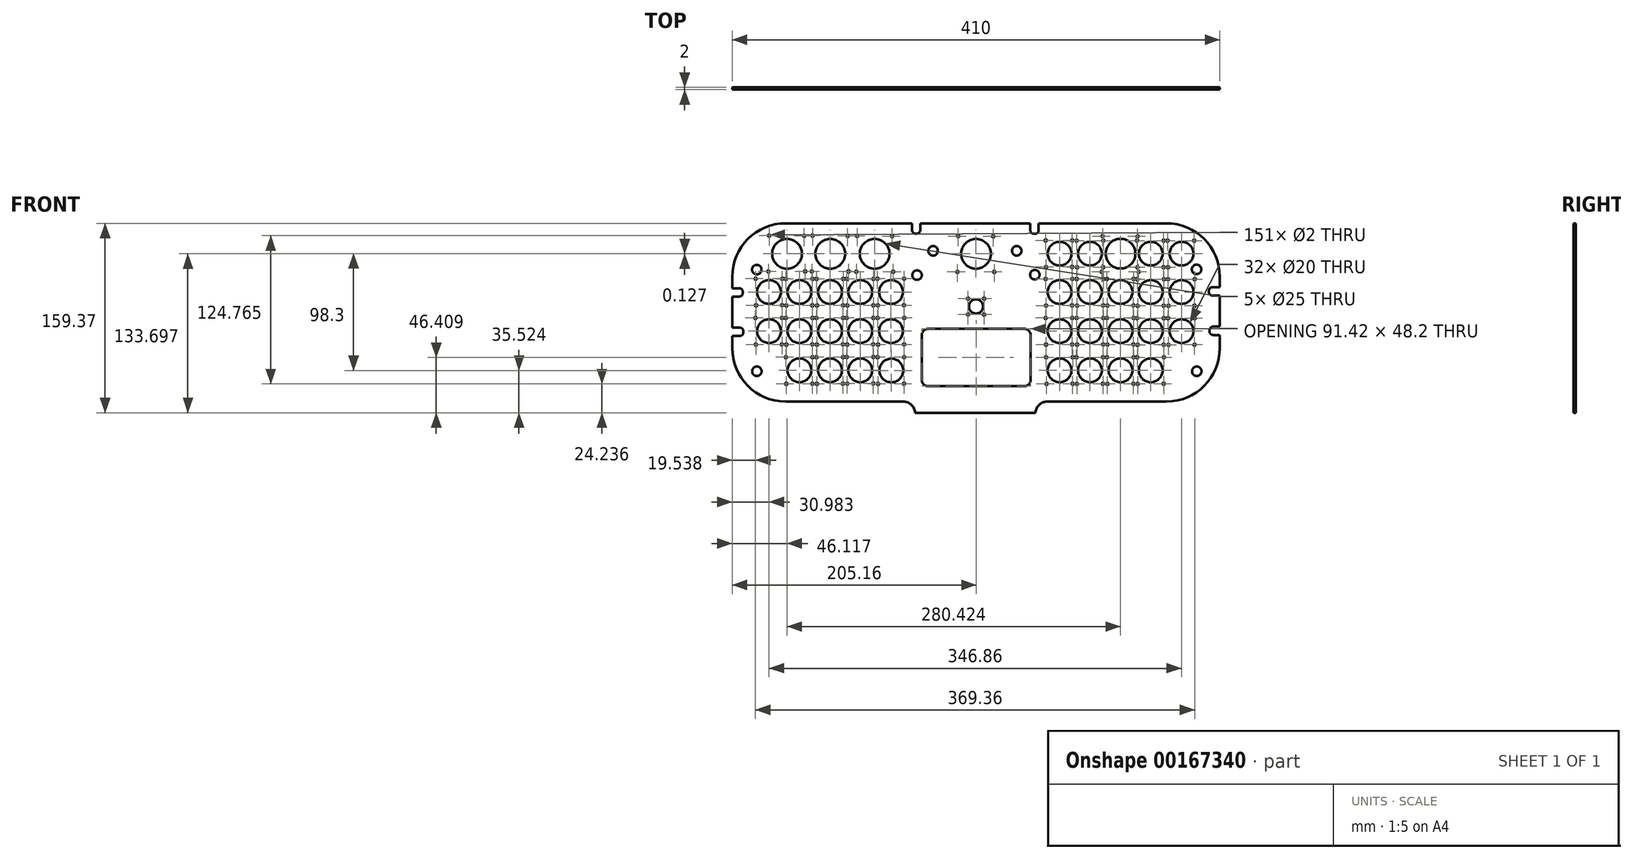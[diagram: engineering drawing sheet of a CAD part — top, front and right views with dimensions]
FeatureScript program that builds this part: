
annotation { "Feature Type Name" : "Feature", "Feature Type Description" : "" }
export const myFeature = defineFeature(function(context is Context, id is Id, definition is map)
    precondition{}
    {
        {
            var Q0;
            Q0=qCreatedBy(makeId("Front.planeOp"),FACE);
            var sketch = newSketch(context, id + "F0", { "sketchPlane" : qUnion([Q0])});
            skLineSegment(sketch, "E0.bottom", {"start": v(205, -75) * mm, "end": v(-205, -75) * mm});
            skLineSegment(sketch, "E0.top", {"start": v(205, 75) * mm, "end": v(-205, 75) * mm});
            skLineSegment(sketch, "E0.left", {"start": v(205, -75) * mm, "end": v(205, 75) * mm});
            skLineSegment(sketch, "E0.right", {"start": v(-205, -75) * mm, "end": v(-205, 75) * mm});
            skSolve(sketch);
        }
        {
            var Q0;
            Q0=qSketchRegion(id+"F0",true);
            extrude(context, id + "F1", {"entities" : qUnion([Q0]), "depth" : 1 * mm, "hasSecondDirection" : true, "secondDirectionOppositeDirection" : true, "secondDirectionDepth" : 1 * mm});
        }
        {
            var Q0;
            Q0=makeQuery(id+"F1.opExtrude","SWEPT_EDGE",EDGE,{"disambiguationData":[OSD([sQuery(id+"F0.wireOp",EDGE,"E0.top"),sQuery(id+"F0.wireOp",EDGE,"E0.right")])]});
            var Q1;
            Q1=makeQuery(id+"F1.opExtrude","SWEPT_EDGE",EDGE,{"disambiguationData":[OSD([sQuery(id+"F0.wireOp",EDGE,"E0.bottom"),sQuery(id+"F0.wireOp",EDGE,"E0.right")])]});
            fillet(context, id + "F2", {"entities" : qUnion([Q0, Q1]), "radius" : 45 * mm, "tangentPropagation" : true, "allowEdgeOverflow" : false});
        }
        {
            var Q0;
            Q0=makeQuery(id+"F1.opExtrude","SWEPT_EDGE",EDGE,{"disambiguationData":[OSD([sQuery(id+"F0.wireOp",EDGE,"E0.top"),sQuery(id+"F0.wireOp",EDGE,"E0.left")])]});
            fillet(context, id + "F3", {"entities" : qUnion([Q0]), "radius" : 45 * mm, "tangentPropagation" : true, "allowEdgeOverflow" : false});
        }
        {
            var Q0;
            Q0=makeQuery(id+"F1.opExtrude","SWEPT_EDGE",EDGE,{"disambiguationData":[OSD([sQuery(id+"F0.wireOp",EDGE,"E0.bottom"),sQuery(id+"F0.wireOp",EDGE,"E0.left")])]});
            fillet(context, id + "F4", {"entities" : qUnion([Q0]), "radius" : 45 * mm, "tangentPropagation" : true, "allowEdgeOverflow" : false});
        }
        {
            var Q0;
            Q0=qCreatedBy(makeId("Front.planeOp"),FACE);
            var sketch = newSketch(context, id + "F5", { "sketchPlane" : qUnion([Q0])});
            skLineSegment(sketch, "E1.bottom", {"start": v(-51.28, -63.48) * mm, "end": v(50, -63.48) * mm});
            skLineSegment(sketch, "E1.top", {"start": v(-51.28, -84.37) * mm, "end": v(50, -84.37) * mm});
            skLineSegment(sketch, "E1.left", {"start": v(-51.28, -63.48) * mm, "end": v(-51.28, -84.37) * mm});
            skLineSegment(sketch, "E1.right", {"start": v(50, -63.48) * mm, "end": v(50, -84.37) * mm});
            skSolve(sketch);
        }
        {
            var Q0;
            Q0=qSketchRegion(id+"F5",true);
            extrude(context, id + "F6", {"entities" : qUnion([Q0]), "operationType" : NewBodyOperationType.ADD, "depth" : 1 * mm, "hasSecondDirection" : true, "secondDirectionOppositeDirection" : true, "secondDirectionDepth" : 1 * mm});
        }
        {
            var Q0;
            Q0=makeQuery(id+"F6.boolean.opBoolean","INTERSECT",EDGE,{"derivedFrom":[makeQuery(id+"F1.opExtrude","SWEPT_FACE",FACE,{"disambiguationData":[OSD([sQuery(id+"F0.wireOp",EDGE,"E0.bottom")])]}),makeQuery(id+"F6.opExtrude","SWEPT_FACE",FACE,{"disambiguationData":[OSD([sQuery(id+"F5.wireOp",EDGE,"E1.left")])]})]});
            fillet(context, id + "F7", {"entities" : qUnion([Q0]), "radius" : 10 * mm, "tangentPropagation" : true, "allowEdgeOverflow" : false});
        }
        {
            var Q0;
            Q0=makeQuery(id+"F6.boolean.opBoolean","INTERSECT",EDGE,{"derivedFrom":[makeQuery(id+"F1.opExtrude","SWEPT_FACE",FACE,{"disambiguationData":[OSD([sQuery(id+"F0.wireOp",EDGE,"E0.bottom")])]}),makeQuery(id+"F6.opExtrude","SWEPT_FACE",FACE,{"disambiguationData":[OSD([sQuery(id+"F5.wireOp",EDGE,"E1.right")])]})]});
            fillet(context, id + "F8", {"entities" : qUnion([Q0]), "radius" : 10 * mm, "tangentPropagation" : true, "allowEdgeOverflow" : false});
        }
        {
            var Q0;
            Q0=qCreatedBy(makeId("Front.planeOp"),FACE);
            var sketch = newSketch(context, id + "F9", { "sketchPlane" : qUnion([Q0])});
            skCircle(sketch, "E2", {"center": v(0, 49.33) * mm, "radius": 12.5 * mm});
            skCircle(sketch, "E3", {"center": v(0, 5.03) * mm, "radius": 6 * mm});
            skCircle(sketch, "E4", {"center": v(-158.88, 49.33) * mm, "radius": 12.5 * mm});
            skCircle(sketch, "E5", {"center": v(-122.54, 49.33) * mm, "radius": 12.5 * mm});
            skCircle(sketch, "E6", {"center": v(-85.24, 49.33) * mm, "radius": 12.5 * mm});
            skCircle(sketch, "E7", {"center": v(172.84, 17.2) * mm, "radius": 10 * mm});
            skCircle(sketch, "E8", {"center": v(172.84, -15.76) * mm, "radius": 10 * mm});
            skCircle(sketch, "E9", {"center": v(146.94, -48.73) * mm, "radius": 10 * mm});
            skCircle(sketch, "E10", {"center": v(146.94, 17.2) * mm, "radius": 10 * mm});
            skCircle(sketch, "E11", {"center": v(146.94, -15.76) * mm, "radius": 10 * mm});
            skCircle(sketch, "E12", {"center": v(121.54, -48.73) * mm, "radius": 10 * mm});
            skCircle(sketch, "E13", {"center": v(121.54, 17.2) * mm, "radius": 10 * mm});
            skCircle(sketch, "E14", {"center": v(121.54, -15.76) * mm, "radius": 10 * mm});
            skCircle(sketch, "E15", {"center": v(95.83, -48.73) * mm, "radius": 10 * mm});
            skCircle(sketch, "E16", {"center": v(95.83, 17.2) * mm, "radius": 10 * mm});
            skCircle(sketch, "E17", {"center": v(95.83, -15.76) * mm, "radius": 10 * mm});
            skCircle(sketch, "E18", {"center": v(70.27, -48.73) * mm, "radius": 10 * mm});
            skCircle(sketch, "E19", {"center": v(70.27, 17.2) * mm, "radius": 10 * mm});
            skCircle(sketch, "E20", {"center": v(70.27, -15.76) * mm, "radius": 10 * mm});
            skCircle(sketch, "E21", {"center": v(172.84, 49.45) * mm, "radius": 10 * mm});
            skCircle(sketch, "E22", {"center": v(146.94, 49.45) * mm, "radius": 10 * mm});
            skCircle(sketch, "E23", {"center": v(121.54, 49.45) * mm, "radius": 12.5 * mm});
            skCircle(sketch, "E24", {"center": v(95.83, 49.45) * mm, "radius": 10 * mm});
            skCircle(sketch, "E25", {"center": v(70.27, 49.45) * mm, "radius": 10 * mm});
            skCircle(sketch, "E26", {"center": v(-71.45, 17.2) * mm, "radius": 10 * mm});
            skCircle(sketch, "E27", {"center": v(-71.45, -15.76) * mm, "radius": 10 * mm});
            skCircle(sketch, "E28", {"center": v(-97.35, -48.73) * mm, "radius": 10 * mm});
            skCircle(sketch, "E29", {"center": v(-97.35, 17.2) * mm, "radius": 10 * mm});
            skCircle(sketch, "E30", {"center": v(-97.35, -15.76) * mm, "radius": 10 * mm});
            skCircle(sketch, "E31", {"center": v(-122.75, -48.73) * mm, "radius": 10 * mm});
            skCircle(sketch, "E32", {"center": v(-122.75, 17.2) * mm, "radius": 10 * mm});
            skCircle(sketch, "E33", {"center": v(-122.75, -15.76) * mm, "radius": 10 * mm});
            skCircle(sketch, "E34", {"center": v(-148.46, -48.73) * mm, "radius": 10 * mm});
            skCircle(sketch, "E35", {"center": v(-148.46, 17.2) * mm, "radius": 10 * mm});
            skCircle(sketch, "E36", {"center": v(-148.46, -15.76) * mm, "radius": 10 * mm});
            skCircle(sketch, "E37", {"center": v(-174.02, 17.2) * mm, "radius": 10 * mm});
            skCircle(sketch, "E38", {"center": v(-174.02, -15.76) * mm, "radius": 10 * mm});
            skCircle(sketch, "E39", {"center": v(-71.2, -48.85) * mm, "radius": 10 * mm});
            skLineSegment(sketch, "E40.bottom", {"start": v(-45.55, -13.86) * mm, "end": v(45.87, -13.86) * mm});
            skLineSegment(sketch, "E40.top", {"start": v(-45.55, -62.06) * mm, "end": v(45.87, -62.06) * mm});
            skLineSegment(sketch, "E40.left", {"start": v(-45.55, -13.86) * mm, "end": v(-45.55, -62.06) * mm});
            skLineSegment(sketch, "E40.right", {"start": v(45.87, -13.86) * mm, "end": v(45.87, -62.06) * mm});
            skSolve(sketch);
        }
        {
            var Q0;
            Q0=makeQuery(id+"F6.boolean.opBoolean","MERGE",FACE,{"derivedFrom":[makeQuery(id+"F1.opExtrude","CAP_FACE",FACE,{"disambiguationData":[OSD([sQuery(id+"F0.wireOp",EDGE,"E0.bottom"),sQuery(id+"F0.wireOp",EDGE,"E0.top"),sQuery(id+"F0.wireOp",EDGE,"E0.left"),sQuery(id+"F0.wireOp",EDGE,"E0.right")])],"isStart":false}),makeQuery(id+"F6.opExtrude","CAP_FACE",FACE,{"disambiguationData":[OSD([sQuery(id+"F5.wireOp",EDGE,"E1.bottom"),sQuery(id+"F5.wireOp",EDGE,"E1.top"),sQuery(id+"F5.wireOp",EDGE,"E1.left"),sQuery(id+"F5.wireOp",EDGE,"E1.right")])],"isStart":false})]});
            cPlane(context, id + "F10", {"entities" : qUnion([Q0]), "cplaneType" : CPlaneType.OFFSET, "offset" : 0 * mm, "width" : 150 * mm, "height" : 150 * mm});
        }
        {
            var Q0;
            Q0=qCreatedBy(id+"F10.planeOp",FACE);
            var sketch = newSketch(context, id + "F11", { "sketchPlane" : qUnion([Q0])});
            skLineSegment(sketch, "E41.bottom", {"start": v(-210.38, 20.36) * mm, "end": v(-199.13, 20.36) * mm});
            skLineSegment(sketch, "E41.top", {"start": v(-210.38, 13.36) * mm, "end": v(-199.13, 13.36) * mm});
            skLineSegment(sketch, "E41.left", {"start": v(-213.38, 17.36) * mm, "end": v(-213.38, 16.36) * mm});
            skLineSegment(sketch, "E41.right", {"start": v(-196.13, 17.36) * mm, "end": v(-196.13, 16.36) * mm});
            skPoint(sketch, "E42.visualSharp", {"position": v(-196.13, 20.36) * mm});
            skArc(sketch, "E42.filletArc", {"start": v(-196.13, 17.36) * mm, "mid": v(-197.01, 19.48) * mm, "end": v(-199.13, 20.36) * mm});
            skPoint(sketch, "E43.visualSharp", {"position": v(-196.13, 13.36) * mm});
            skArc(sketch, "E43.filletArc", {"start": v(-199.13, 13.36) * mm, "mid": v(-197.01, 14.23) * mm, "end": v(-196.13, 16.36) * mm});
            skPoint(sketch, "E44.visualSharp", {"position": v(-213.38, 20.36) * mm});
            skArc(sketch, "E44.filletArc", {"start": v(-210.38, 20.36) * mm, "mid": v(-212.5, 19.48) * mm, "end": v(-213.38, 17.36) * mm});
            skPoint(sketch, "E45.visualSharp", {"position": v(-213.38, 13.36) * mm});
            skArc(sketch, "E45.filletArc", {"start": v(-213.38, 16.36) * mm, "mid": v(-212.5, 14.23) * mm, "end": v(-210.38, 13.36) * mm});
            skLineSegment(sketch, "E46.bottom", {"start": v(-209.84, -12.8) * mm, "end": v(-198.59, -12.8) * mm});
            skLineSegment(sketch, "E46.top", {"start": v(-209.84, -19.8) * mm, "end": v(-198.59, -19.8) * mm});
            skLineSegment(sketch, "E46.left", {"start": v(-212.84, -15.8) * mm, "end": v(-212.84, -16.8) * mm});
            skLineSegment(sketch, "E46.right", {"start": v(-195.59, -15.8) * mm, "end": v(-195.59, -16.8) * mm});
            skPoint(sketch, "E47.visualSharp", {"position": v(-195.59, -12.8) * mm});
            skArc(sketch, "E47.filletArc", {"start": v(-195.59, -15.8) * mm, "mid": v(-196.47, -13.69) * mm, "end": v(-198.59, -12.8) * mm});
            skPoint(sketch, "E48.visualSharp", {"position": v(-195.59, -19.8) * mm});
            skArc(sketch, "E48.filletArc", {"start": v(-198.59, -19.8) * mm, "mid": v(-196.47, -18.93) * mm, "end": v(-195.59, -16.8) * mm});
            skPoint(sketch, "E49.visualSharp", {"position": v(-212.84, -12.8) * mm});
            skArc(sketch, "E49.filletArc", {"start": v(-209.84, -12.8) * mm, "mid": v(-211.96, -13.69) * mm, "end": v(-212.84, -15.8) * mm});
            skPoint(sketch, "E50.visualSharp", {"position": v(-212.84, -19.8) * mm});
            skArc(sketch, "E50.filletArc", {"start": v(-212.84, -16.8) * mm, "mid": v(-211.96, -18.93) * mm, "end": v(-209.84, -19.8) * mm});
            skLineSegment(sketch, "E51.bottom", {"start": v(198.82, 21.2) * mm, "end": v(210.07, 21.2) * mm});
            skLineSegment(sketch, "E51.top", {"start": v(198.82, 14.2) * mm, "end": v(210.07, 14.2) * mm});
            skLineSegment(sketch, "E51.left", {"start": v(195.82, 18.2) * mm, "end": v(195.82, 17.2) * mm});
            skLineSegment(sketch, "E51.right", {"start": v(213.07, 18.2) * mm, "end": v(213.07, 17.2) * mm});
            skPoint(sketch, "E52.visualSharp", {"position": v(213.07, 21.2) * mm});
            skArc(sketch, "E52.filletArc", {"start": v(213.07, 18.2) * mm, "mid": v(212.2, 20.32) * mm, "end": v(210.07, 21.2) * mm});
            skPoint(sketch, "E53.visualSharp", {"position": v(213.07, 14.2) * mm});
            skArc(sketch, "E53.filletArc", {"start": v(210.07, 14.2) * mm, "mid": v(212.2, 15.07) * mm, "end": v(213.07, 17.2) * mm});
            skPoint(sketch, "E54.visualSharp", {"position": v(195.82, 21.2) * mm});
            skArc(sketch, "E54.filletArc", {"start": v(198.82, 21.2) * mm, "mid": v(196.7, 20.32) * mm, "end": v(195.82, 18.2) * mm});
            skPoint(sketch, "E55.visualSharp", {"position": v(195.82, 14.2) * mm});
            skArc(sketch, "E55.filletArc", {"start": v(195.82, 17.2) * mm, "mid": v(196.7, 15.07) * mm, "end": v(198.82, 14.2) * mm});
            skLineSegment(sketch, "E56.bottom", {"start": v(199.36, -11.97) * mm, "end": v(210.61, -11.97) * mm});
            skLineSegment(sketch, "E56.top", {"start": v(199.36, -18.97) * mm, "end": v(210.61, -18.97) * mm});
            skLineSegment(sketch, "E56.left", {"start": v(196.36, -14.97) * mm, "end": v(196.36, -15.97) * mm});
            skLineSegment(sketch, "E56.right", {"start": v(213.61, -14.97) * mm, "end": v(213.61, -15.97) * mm});
            skPoint(sketch, "E57.visualSharp", {"position": v(213.61, -11.97) * mm});
            skArc(sketch, "E57.filletArc", {"start": v(213.61, -14.97) * mm, "mid": v(212.73, -12.85) * mm, "end": v(210.61, -11.97) * mm});
            skPoint(sketch, "E58.visualSharp", {"position": v(213.61, -18.97) * mm});
            skArc(sketch, "E58.filletArc", {"start": v(210.61, -18.97) * mm, "mid": v(212.73, -18.1) * mm, "end": v(213.61, -15.97) * mm});
            skPoint(sketch, "E59.visualSharp", {"position": v(196.36, -11.97) * mm});
            skArc(sketch, "E59.filletArc", {"start": v(199.36, -11.97) * mm, "mid": v(197.24, -12.85) * mm, "end": v(196.36, -14.97) * mm});
            skPoint(sketch, "E60.visualSharp", {"position": v(196.36, -18.97) * mm});
            skArc(sketch, "E60.filletArc", {"start": v(196.36, -15.97) * mm, "mid": v(197.24, -18.1) * mm, "end": v(199.36, -18.97) * mm});
            skLineSegment(sketch, "E61.bottom", {"start": v(-50.84, 85.12) * mm, "end": v(-49.84, 85.12) * mm});
            skLineSegment(sketch, "E61.top", {"start": v(-50.84, 66.34) * mm, "end": v(-49.84, 66.34) * mm});
            skLineSegment(sketch, "E61.left", {"start": v(-53.84, 82.12) * mm, "end": v(-53.84, 69.34) * mm});
            skLineSegment(sketch, "E61.right", {"start": v(-46.84, 82.12) * mm, "end": v(-46.84, 69.34) * mm});
            skPoint(sketch, "E62.visualSharp", {"position": v(-53.84, 85.12) * mm});
            skArc(sketch, "E62.filletArc", {"start": v(-50.84, 85.12) * mm, "mid": v(-52.96, 84.24) * mm, "end": v(-53.84, 82.12) * mm});
            skPoint(sketch, "E63.visualSharp", {"position": v(-46.84, 85.12) * mm});
            skArc(sketch, "E63.filletArc", {"start": v(-46.84, 82.12) * mm, "mid": v(-47.72, 84.24) * mm, "end": v(-49.84, 85.12) * mm});
            skPoint(sketch, "E64.visualSharp", {"position": v(-46.84, 66.34) * mm});
            skArc(sketch, "E64.filletArc", {"start": v(-49.84, 66.34) * mm, "mid": v(-47.72, 67.22) * mm, "end": v(-46.84, 69.34) * mm});
            skPoint(sketch, "E65.visualSharp", {"position": v(-53.84, 66.34) * mm});
            skArc(sketch, "E65.filletArc", {"start": v(-53.84, 69.34) * mm, "mid": v(-52.96, 67.22) * mm, "end": v(-50.84, 66.34) * mm});
            skLineSegment(sketch, "E66.bottom", {"start": v(48.7, 84.97) * mm, "end": v(49.7, 84.97) * mm});
            skLineSegment(sketch, "E66.top", {"start": v(48.7, 66.19) * mm, "end": v(49.7, 66.19) * mm});
            skLineSegment(sketch, "E66.left", {"start": v(45.7, 81.97) * mm, "end": v(45.7, 69.19) * mm});
            skLineSegment(sketch, "E66.right", {"start": v(52.7, 81.97) * mm, "end": v(52.7, 69.19) * mm});
            skPoint(sketch, "E67.visualSharp", {"position": v(45.7, 84.97) * mm});
            skArc(sketch, "E67.filletArc", {"start": v(48.7, 84.97) * mm, "mid": v(46.57, 84.09) * mm, "end": v(45.7, 81.97) * mm});
            skPoint(sketch, "E68.visualSharp", {"position": v(52.7, 84.97) * mm});
            skArc(sketch, "E68.filletArc", {"start": v(52.7, 81.97) * mm, "mid": v(51.81, 84.09) * mm, "end": v(49.7, 84.97) * mm});
            skPoint(sketch, "E69.visualSharp", {"position": v(52.7, 66.19) * mm});
            skArc(sketch, "E69.filletArc", {"start": v(49.7, 66.19) * mm, "mid": v(51.81, 67.07) * mm, "end": v(52.7, 69.19) * mm});
            skPoint(sketch, "E70.visualSharp", {"position": v(45.7, 66.19) * mm});
            skArc(sketch, "E70.filletArc", {"start": v(45.7, 69.19) * mm, "mid": v(46.57, 67.07) * mm, "end": v(48.7, 66.19) * mm});
            skSolve(sketch);
        }
        {
            var Q0;
            Q0=makeQuery(id+"F6.boolean.opBoolean","MERGE",FACE,{"derivedFrom":[makeQuery(id+"F1.opExtrude","CAP_FACE",FACE,{"disambiguationData":[OSD([sQuery(id+"F0.wireOp",EDGE,"E0.bottom"),sQuery(id+"F0.wireOp",EDGE,"E0.top"),sQuery(id+"F0.wireOp",EDGE,"E0.left"),sQuery(id+"F0.wireOp",EDGE,"E0.right")])],"isStart":false}),makeQuery(id+"F6.opExtrude","CAP_FACE",FACE,{"disambiguationData":[OSD([sQuery(id+"F5.wireOp",EDGE,"E1.bottom"),sQuery(id+"F5.wireOp",EDGE,"E1.top"),sQuery(id+"F5.wireOp",EDGE,"E1.left"),sQuery(id+"F5.wireOp",EDGE,"E1.right")])],"isStart":false})]});
            cPlane(context, id + "F12", {"entities" : qUnion([Q0]), "cplaneType" : CPlaneType.OFFSET, "offset" : 2 * mm, "oppositeDirection" : true, "width" : 150 * mm, "height" : 150 * mm});
        }
        {
            var Q0;
            Q0=qCreatedBy(id+"F12.planeOp",FACE);
            var sketch = newSketch(context, id + "F13", { "sketchPlane" : qUnion([Q0])});
            skCircle(sketch, "E71", {"center": v(-184.3, 36.01) * mm, "radius": 4 * mm});
            skCircle(sketch, "E72", {"center": v(-184.28, -49.46) * mm, "radius": 4 * mm});
            skCircle(sketch, "E73", {"center": v(-36.07, 51.83) * mm, "radius": 4 * mm});
            skCircle(sketch, "E74", {"center": v(-49.57, 31.39) * mm, "radius": 4 * mm});
            skCircle(sketch, "E75", {"center": v(34.27, 51.83) * mm, "radius": 4 * mm});
            skCircle(sketch, "E76", {"center": v(49.46, 31.76) * mm, "radius": 4 * mm});
            skCircle(sketch, "E77", {"center": v(185.45, 36.26) * mm, "radius": 4 * mm});
            skCircle(sketch, "E78", {"center": v(185.64, -49.46) * mm, "radius": 4 * mm});
            skSolve(sketch);
        }
        {
            var Q0;
            Q0=qSketchRegion(id+"F13",true);
            extrude(context, id + "F14", {"entities" : qUnion([Q0]), "operationType" : NewBodyOperationType.REMOVE, "depth" : 28.49 * mm, "hasSecondDirection" : true, "secondDirectionOppositeDirection" : true, "secondDirectionDepth" : 25 * mm});
        }
        {
            var Q0;
            Q0=qSketchRegion(id+"F9",true);
            extrude(context, id + "F15", {"entities" : qUnion([Q0]), "operationType" : NewBodyOperationType.REMOVE, "depth" : 25 * mm, "hasSecondDirection" : true, "secondDirectionOppositeDirection" : true, "secondDirectionDepth" : 25 * mm});
        }
        {
            var Q0;
            Q0=qSketchRegion(id+"F11",true);
            extrude(context, id + "F16", {"entities" : qUnion([Q0]), "operationType" : NewBodyOperationType.REMOVE, "oppositeDirection" : true, "depth" : 50 * mm, "hasSecondDirection" : true, "secondDirectionOppositeDirection" : false, "secondDirectionDepth" : 50 * mm});
        }
        {
            var Q0;
            Q0=makeQuery(id+"F6.boolean.opBoolean","MERGE",FACE,{"derivedFrom":[makeQuery(id+"F1.opExtrude","CAP_FACE",FACE,{"disambiguationData":[OSD([sQuery(id+"F0.wireOp",EDGE,"E0.bottom"),sQuery(id+"F0.wireOp",EDGE,"E0.top"),sQuery(id+"F0.wireOp",EDGE,"E0.left"),sQuery(id+"F0.wireOp",EDGE,"E0.right")])],"isStart":true}),makeQuery(id+"F6.opExtrude","CAP_FACE",FACE,{"disambiguationData":[OSD([sQuery(id+"F5.wireOp",EDGE,"E1.bottom"),sQuery(id+"F5.wireOp",EDGE,"E1.top"),sQuery(id+"F5.wireOp",EDGE,"E1.left"),sQuery(id+"F5.wireOp",EDGE,"E1.right")])],"isStart":true})]});
            cPlane(context, id + "F17", {"entities" : qUnion([Q0]), "cplaneType" : CPlaneType.OFFSET, "offset" : 0 * mm, "oppositeDirection" : true, "width" : 150 * mm, "height" : 150 * mm});
        }
        {
            var Q0;
            Q0=qCreatedBy(id+"F17.planeOp",FACE);
            var sketch = newSketch(context, id + "F18", { "sketchPlane" : qUnion([Q0])});
            skLineSegment(sketch, "E79.bottom", {"start": v(184.07, 27.38) * mm, "end": v(163.8, 27.38) * mm, "construction": true});
            skLineSegment(sketch, "E79.top", {"start": v(184.07, 7.22) * mm, "end": v(163.8, 7.22) * mm, "construction": true});
            skLineSegment(sketch, "E79.left", {"start": v(184.07, 27.38) * mm, "end": v(184.07, 7.22) * mm, "construction": true});
            skLineSegment(sketch, "E79.right", {"start": v(163.8, 27.38) * mm, "end": v(163.8, 7.22) * mm, "construction": true});
            skPoint(sketch, "E80", {"position": v(185.32, 28.38) * mm});
            skPoint(sketch, "E81", {"position": v(162.91, 28.38) * mm});
            skPoint(sketch, "E82", {"position": v(184.95, 5.97) * mm});
            skPoint(sketch, "E83", {"position": v(163.04, 6.1) * mm});
            skLineSegment(sketch, "E84.bottom", {"start": v(158.64, 27.26) * mm, "end": v(138.36, 27.26) * mm, "construction": true});
            skLineSegment(sketch, "E84.top", {"start": v(158.64, 7.1) * mm, "end": v(138.36, 7.1) * mm, "construction": true});
            skLineSegment(sketch, "E84.left", {"start": v(158.64, 27.26) * mm, "end": v(158.64, 7.1) * mm, "construction": true});
            skLineSegment(sketch, "E84.right", {"start": v(138.36, 27.26) * mm, "end": v(138.36, 7.1) * mm, "construction": true});
            skPoint(sketch, "E85", {"position": v(159.89, 28.26) * mm});
            skPoint(sketch, "E86", {"position": v(137.48, 28.26) * mm});
            skPoint(sketch, "E87", {"position": v(159.51, 5.85) * mm});
            skPoint(sketch, "E88", {"position": v(137.6, 5.98) * mm});
            skLineSegment(sketch, "E89.bottom", {"start": v(132.78, 27.26) * mm, "end": v(112.5, 27.26) * mm, "construction": true});
            skLineSegment(sketch, "E89.top", {"start": v(132.78, 7.1) * mm, "end": v(112.5, 7.1) * mm, "construction": true});
            skLineSegment(sketch, "E89.left", {"start": v(132.78, 27.26) * mm, "end": v(132.78, 7.1) * mm, "construction": true});
            skLineSegment(sketch, "E89.right", {"start": v(112.5, 27.26) * mm, "end": v(112.5, 7.1) * mm, "construction": true});
            skPoint(sketch, "E90", {"position": v(134.03, 28.26) * mm});
            skPoint(sketch, "E91", {"position": v(111.62, 28.26) * mm});
            skPoint(sketch, "E92", {"position": v(133.66, 5.85) * mm});
            skPoint(sketch, "E93", {"position": v(111.75, 5.98) * mm});
            skLineSegment(sketch, "E94.bottom", {"start": v(107.35, 27.26) * mm, "end": v(87.07, 27.26) * mm, "construction": true});
            skLineSegment(sketch, "E94.top", {"start": v(107.35, 7.1) * mm, "end": v(87.07, 7.1) * mm, "construction": true});
            skLineSegment(sketch, "E94.left", {"start": v(107.35, 27.26) * mm, "end": v(107.35, 7.1) * mm, "construction": true});
            skLineSegment(sketch, "E94.right", {"start": v(87.07, 27.26) * mm, "end": v(87.07, 7.1) * mm, "construction": true});
            skPoint(sketch, "E95", {"position": v(108.6, 28.26) * mm});
            skPoint(sketch, "E96", {"position": v(86.19, 28.26) * mm});
            skPoint(sketch, "E97", {"position": v(108.22, 5.85) * mm});
            skPoint(sketch, "E98", {"position": v(86.31, 5.98) * mm});
            skLineSegment(sketch, "E99.bottom", {"start": v(81.63, 27.4) * mm, "end": v(61.35, 27.4) * mm, "construction": true});
            skLineSegment(sketch, "E99.top", {"start": v(81.63, 7.24) * mm, "end": v(61.35, 7.24) * mm, "construction": true});
            skLineSegment(sketch, "E99.left", {"start": v(81.63, 27.4) * mm, "end": v(81.63, 7.24) * mm, "construction": true});
            skLineSegment(sketch, "E99.right", {"start": v(61.35, 27.4) * mm, "end": v(61.35, 7.24) * mm, "construction": true});
            skPoint(sketch, "E100", {"position": v(82.88, 28.4) * mm});
            skPoint(sketch, "E101", {"position": v(60.47, 28.4) * mm});
            skPoint(sketch, "E102", {"position": v(82.5, 6) * mm});
            skPoint(sketch, "E103", {"position": v(60.6, 6.12) * mm});
            skLineSegment(sketch, "E104.bottom", {"start": v(184.21, -5.62) * mm, "end": v(163.93, -5.62) * mm, "construction": true});
            skLineSegment(sketch, "E104.top", {"start": v(184.21, -25.78) * mm, "end": v(163.93, -25.78) * mm, "construction": true});
            skLineSegment(sketch, "E104.left", {"start": v(184.21, -5.62) * mm, "end": v(184.21, -25.78) * mm, "construction": true});
            skLineSegment(sketch, "E104.right", {"start": v(163.93, -5.62) * mm, "end": v(163.93, -25.78) * mm, "construction": true});
            skPoint(sketch, "E105", {"position": v(185.46, -4.62) * mm});
            skPoint(sketch, "E106", {"position": v(163.05, -4.62) * mm});
            skPoint(sketch, "E107", {"position": v(185.09, -27.03) * mm});
            skPoint(sketch, "E108", {"position": v(163.18, -26.9) * mm});
            skLineSegment(sketch, "E109.bottom", {"start": v(158.64, -5.62) * mm, "end": v(138.36, -5.62) * mm, "construction": true});
            skLineSegment(sketch, "E109.top", {"start": v(158.64, -25.78) * mm, "end": v(138.36, -25.78) * mm, "construction": true});
            skLineSegment(sketch, "E109.left", {"start": v(158.64, -5.62) * mm, "end": v(158.64, -25.78) * mm, "construction": true});
            skLineSegment(sketch, "E109.right", {"start": v(138.36, -5.62) * mm, "end": v(138.36, -25.78) * mm, "construction": true});
            skPoint(sketch, "E110", {"position": v(159.89, -4.62) * mm});
            skPoint(sketch, "E111", {"position": v(137.48, -4.62) * mm});
            skPoint(sketch, "E112", {"position": v(159.51, -27.03) * mm});
            skPoint(sketch, "E113", {"position": v(137.6, -26.9) * mm});
            skLineSegment(sketch, "E114.bottom", {"start": v(132.92, -5.62) * mm, "end": v(112.64, -5.62) * mm, "construction": true});
            skLineSegment(sketch, "E114.top", {"start": v(132.92, -25.78) * mm, "end": v(112.64, -25.78) * mm, "construction": true});
            skLineSegment(sketch, "E114.left", {"start": v(132.92, -5.62) * mm, "end": v(132.92, -25.78) * mm, "construction": true});
            skLineSegment(sketch, "E114.right", {"start": v(112.64, -5.62) * mm, "end": v(112.64, -25.78) * mm, "construction": true});
            skPoint(sketch, "E115", {"position": v(134.17, -4.62) * mm});
            skPoint(sketch, "E116", {"position": v(111.76, -4.62) * mm});
            skPoint(sketch, "E117", {"position": v(133.8, -27.03) * mm});
            skPoint(sketch, "E118", {"position": v(111.89, -26.9) * mm});
            skLineSegment(sketch, "E119.bottom", {"start": v(107.49, -5.62) * mm, "end": v(87.2, -5.62) * mm, "construction": true});
            skLineSegment(sketch, "E119.top", {"start": v(107.49, -25.78) * mm, "end": v(87.2, -25.78) * mm, "construction": true});
            skLineSegment(sketch, "E119.left", {"start": v(107.49, -5.62) * mm, "end": v(107.49, -25.78) * mm, "construction": true});
            skLineSegment(sketch, "E119.right", {"start": v(87.2, -5.62) * mm, "end": v(87.2, -25.78) * mm, "construction": true});
            skPoint(sketch, "E120", {"position": v(108.74, -4.62) * mm});
            skPoint(sketch, "E121", {"position": v(86.33, -4.62) * mm});
            skPoint(sketch, "E122", {"position": v(108.36, -27.03) * mm});
            skPoint(sketch, "E123", {"position": v(86.45, -26.9) * mm});
            skLineSegment(sketch, "E124.bottom", {"start": v(81.5, -5.62) * mm, "end": v(61.2, -5.62) * mm, "construction": true});
            skLineSegment(sketch, "E124.top", {"start": v(81.5, -25.78) * mm, "end": v(61.2, -25.78) * mm, "construction": true});
            skLineSegment(sketch, "E124.left", {"start": v(81.5, -5.62) * mm, "end": v(81.5, -25.78) * mm, "construction": true});
            skLineSegment(sketch, "E124.right", {"start": v(61.2, -5.62) * mm, "end": v(61.2, -25.78) * mm, "construction": true});
            skPoint(sketch, "E125", {"position": v(82.74, -4.62) * mm});
            skPoint(sketch, "E126", {"position": v(60.33, -4.62) * mm});
            skPoint(sketch, "E127", {"position": v(82.37, -27.03) * mm});
            skPoint(sketch, "E128", {"position": v(60.46, -26.9) * mm});
            skLineSegment(sketch, "E129.bottom", {"start": v(158.65, -38.7) * mm, "end": v(138.37, -38.7) * mm, "construction": true});
            skLineSegment(sketch, "E129.top", {"start": v(158.65, -58.85) * mm, "end": v(138.37, -58.85) * mm, "construction": true});
            skLineSegment(sketch, "E129.left", {"start": v(158.65, -38.7) * mm, "end": v(158.65, -58.85) * mm, "construction": true});
            skLineSegment(sketch, "E129.right", {"start": v(138.37, -38.7) * mm, "end": v(138.37, -58.85) * mm, "construction": true});
            skPoint(sketch, "E130", {"position": v(159.9, -37.69) * mm});
            skPoint(sketch, "E131", {"position": v(137.5, -37.69) * mm});
            skPoint(sketch, "E132", {"position": v(159.53, -60.1) * mm});
            skPoint(sketch, "E133", {"position": v(137.62, -59.97) * mm});
            skLineSegment(sketch, "E134.bottom", {"start": v(132.95, -38.7) * mm, "end": v(112.67, -38.7) * mm, "construction": true});
            skLineSegment(sketch, "E134.top", {"start": v(132.95, -58.85) * mm, "end": v(112.67, -58.85) * mm, "construction": true});
            skLineSegment(sketch, "E134.left", {"start": v(132.95, -38.7) * mm, "end": v(132.95, -58.85) * mm, "construction": true});
            skLineSegment(sketch, "E134.right", {"start": v(112.67, -38.7) * mm, "end": v(112.67, -58.85) * mm, "construction": true});
            skPoint(sketch, "E135", {"position": v(134.2, -37.69) * mm});
            skPoint(sketch, "E136", {"position": v(111.8, -37.69) * mm});
            skPoint(sketch, "E137", {"position": v(133.83, -60.1) * mm});
            skPoint(sketch, "E138", {"position": v(111.92, -59.97) * mm});
            skLineSegment(sketch, "E139.bottom", {"start": v(107.44, -38.5) * mm, "end": v(87.16, -38.5) * mm, "construction": true});
            skLineSegment(sketch, "E139.top", {"start": v(107.44, -58.66) * mm, "end": v(87.16, -58.66) * mm, "construction": true});
            skLineSegment(sketch, "E139.left", {"start": v(107.44, -38.5) * mm, "end": v(107.44, -58.66) * mm, "construction": true});
            skLineSegment(sketch, "E139.right", {"start": v(87.16, -38.5) * mm, "end": v(87.16, -58.66) * mm, "construction": true});
            skPoint(sketch, "E140", {"position": v(108.7, -37.5) * mm});
            skPoint(sketch, "E141", {"position": v(86.29, -37.5) * mm});
            skPoint(sketch, "E142", {"position": v(108.32, -59.91) * mm});
            skPoint(sketch, "E143", {"position": v(86.41, -59.79) * mm});
            skLineSegment(sketch, "E144.bottom", {"start": v(81.56, -38.7) * mm, "end": v(61.28, -38.7) * mm, "construction": true});
            skLineSegment(sketch, "E144.top", {"start": v(81.56, -58.85) * mm, "end": v(61.28, -58.85) * mm, "construction": true});
            skLineSegment(sketch, "E144.left", {"start": v(81.56, -38.7) * mm, "end": v(81.56, -58.85) * mm, "construction": true});
            skLineSegment(sketch, "E144.right", {"start": v(61.28, -38.7) * mm, "end": v(61.28, -58.85) * mm, "construction": true});
            skPoint(sketch, "E145", {"position": v(82.8, -37.69) * mm});
            skPoint(sketch, "E146", {"position": v(60.4, -37.69) * mm});
            skPoint(sketch, "E147", {"position": v(82.43, -60.1) * mm});
            skPoint(sketch, "E148", {"position": v(60.53, -59.97) * mm});
            skLineSegment(sketch, "E149.bottom", {"start": v(-59.78, 59.6) * mm, "end": v(-80.07, 59.6) * mm, "construction": true});
            skLineSegment(sketch, "E149.top", {"start": v(-59.78, 39.44) * mm, "end": v(-80.07, 39.44) * mm, "construction": true});
            skLineSegment(sketch, "E149.left", {"start": v(-59.78, 59.6) * mm, "end": v(-59.78, 39.44) * mm, "construction": true});
            skLineSegment(sketch, "E149.right", {"start": v(-80.07, 59.6) * mm, "end": v(-80.07, 39.44) * mm, "construction": true});
            skPoint(sketch, "E150", {"position": v(-58.53, 60.6) * mm});
            skPoint(sketch, "E151", {"position": v(-80.94, 60.6) * mm});
            skPoint(sketch, "E152", {"position": v(-58.9, 38.19) * mm});
            skPoint(sketch, "E153", {"position": v(-80.82, 38.31) * mm});
            skLineSegment(sketch, "E154.bottom", {"start": v(-85.9, 59.39) * mm, "end": v(-106.17, 59.39) * mm, "construction": true});
            skLineSegment(sketch, "E154.top", {"start": v(-85.9, 39.23) * mm, "end": v(-106.17, 39.23) * mm, "construction": true});
            skLineSegment(sketch, "E154.left", {"start": v(-85.9, 59.39) * mm, "end": v(-85.9, 39.23) * mm, "construction": true});
            skLineSegment(sketch, "E154.right", {"start": v(-106.17, 59.39) * mm, "end": v(-106.17, 39.23) * mm, "construction": true});
            skPoint(sketch, "E155", {"position": v(-84.64, 60.39) * mm});
            skPoint(sketch, "E156", {"position": v(-107.05, 60.39) * mm});
            skPoint(sketch, "E157", {"position": v(-85.02, 37.98) * mm});
            skPoint(sketch, "E158", {"position": v(-106.92, 38.1) * mm});
            skLineSegment(sketch, "E159.bottom", {"start": v(-136.63, 59.39) * mm, "end": v(-156.91, 59.39) * mm, "construction": true});
            skLineSegment(sketch, "E159.top", {"start": v(-136.63, 39.23) * mm, "end": v(-156.91, 39.23) * mm, "construction": true});
            skLineSegment(sketch, "E159.left", {"start": v(-136.63, 59.39) * mm, "end": v(-136.63, 39.23) * mm, "construction": true});
            skLineSegment(sketch, "E159.right", {"start": v(-156.91, 59.39) * mm, "end": v(-156.91, 39.23) * mm, "construction": true});
            skPoint(sketch, "E160", {"position": v(-135.38, 60.39) * mm});
            skPoint(sketch, "E161", {"position": v(-157.79, 60.39) * mm});
            skPoint(sketch, "E162", {"position": v(-135.76, 37.98) * mm});
            skPoint(sketch, "E163", {"position": v(-157.66, 38.1) * mm});
            skLineSegment(sketch, "E164.bottom", {"start": v(-162.32, 59.39) * mm, "end": v(-182.6, 59.39) * mm, "construction": true});
            skLineSegment(sketch, "E164.top", {"start": v(-162.32, 39.23) * mm, "end": v(-182.6, 39.23) * mm, "construction": true});
            skLineSegment(sketch, "E164.left", {"start": v(-162.32, 59.39) * mm, "end": v(-162.32, 39.23) * mm, "construction": true});
            skLineSegment(sketch, "E164.right", {"start": v(-182.6, 59.39) * mm, "end": v(-182.6, 39.23) * mm, "construction": true});
            skPoint(sketch, "E165", {"position": v(-161.07, 60.39) * mm});
            skPoint(sketch, "E166", {"position": v(-183.48, 60.39) * mm});
            skPoint(sketch, "E167", {"position": v(-161.44, 37.98) * mm});
            skPoint(sketch, "E168", {"position": v(-183.35, 38.1) * mm});
            skLineSegment(sketch, "E169.bottom", {"start": v(-59.78, 27.17) * mm, "end": v(-80.07, 27.17) * mm, "construction": true});
            skLineSegment(sketch, "E169.top", {"start": v(-59.78, 7.02) * mm, "end": v(-80.07, 7.02) * mm, "construction": true});
            skLineSegment(sketch, "E169.left", {"start": v(-59.78, 27.17) * mm, "end": v(-59.78, 7.02) * mm, "construction": true});
            skLineSegment(sketch, "E169.right", {"start": v(-80.07, 27.17) * mm, "end": v(-80.07, 7.02) * mm, "construction": true});
            skPoint(sketch, "E170", {"position": v(-58.53, 28.17) * mm});
            skPoint(sketch, "E171", {"position": v(-80.94, 28.17) * mm});
            skPoint(sketch, "E172", {"position": v(-58.9, 5.77) * mm});
            skPoint(sketch, "E173", {"position": v(-80.82, 5.9) * mm});
            skLineSegment(sketch, "E174.bottom", {"start": v(-85.9, 27.17) * mm, "end": v(-106.17, 27.17) * mm, "construction": true});
            skLineSegment(sketch, "E174.top", {"start": v(-85.9, 7.02) * mm, "end": v(-106.17, 7.02) * mm, "construction": true});
            skLineSegment(sketch, "E174.left", {"start": v(-85.9, 27.17) * mm, "end": v(-85.9, 7.02) * mm, "construction": true});
            skLineSegment(sketch, "E174.right", {"start": v(-106.17, 27.17) * mm, "end": v(-106.17, 7.02) * mm, "construction": true});
            skPoint(sketch, "E175", {"position": v(-84.64, 28.17) * mm});
            skPoint(sketch, "E176", {"position": v(-107.05, 28.17) * mm});
            skPoint(sketch, "E177", {"position": v(-85.02, 5.77) * mm});
            skPoint(sketch, "E178", {"position": v(-106.92, 5.9) * mm});
            skLineSegment(sketch, "E179.bottom", {"start": v(-111.37, 27.17) * mm, "end": v(-131.65, 27.17) * mm, "construction": true});
            skLineSegment(sketch, "E179.top", {"start": v(-111.37, 7.02) * mm, "end": v(-131.65, 7.02) * mm, "construction": true});
            skLineSegment(sketch, "E179.left", {"start": v(-111.37, 27.17) * mm, "end": v(-111.37, 7.02) * mm, "construction": true});
            skLineSegment(sketch, "E179.right", {"start": v(-131.65, 27.17) * mm, "end": v(-131.65, 7.02) * mm, "construction": true});
            skPoint(sketch, "E180", {"position": v(-110.12, 28.17) * mm});
            skPoint(sketch, "E181", {"position": v(-132.52, 28.17) * mm});
            skPoint(sketch, "E182", {"position": v(-110.5, 5.77) * mm});
            skPoint(sketch, "E183", {"position": v(-132.4, 5.9) * mm});
            skLineSegment(sketch, "E184.bottom", {"start": v(-136.84, 26.96) * mm, "end": v(-157.12, 26.96) * mm, "construction": true});
            skLineSegment(sketch, "E184.top", {"start": v(-136.84, 6.8) * mm, "end": v(-157.12, 6.8) * mm, "construction": true});
            skLineSegment(sketch, "E184.left", {"start": v(-136.84, 26.96) * mm, "end": v(-136.84, 6.8) * mm, "construction": true});
            skLineSegment(sketch, "E184.right", {"start": v(-157.12, 26.96) * mm, "end": v(-157.12, 6.8) * mm, "construction": true});
            skPoint(sketch, "E185", {"position": v(-135.6, 27.96) * mm});
            skPoint(sketch, "E186", {"position": v(-158, 27.96) * mm});
            skPoint(sketch, "E187", {"position": v(-135.97, 5.56) * mm});
            skPoint(sketch, "E188", {"position": v(-157.88, 5.68) * mm});
            skLineSegment(sketch, "E189.bottom", {"start": v(-162.74, 26.96) * mm, "end": v(-183.02, 26.96) * mm, "construction": true});
            skLineSegment(sketch, "E189.top", {"start": v(-162.74, 6.8) * mm, "end": v(-183.02, 6.8) * mm, "construction": true});
            skLineSegment(sketch, "E189.left", {"start": v(-162.74, 26.96) * mm, "end": v(-162.74, 6.8) * mm, "construction": true});
            skLineSegment(sketch, "E189.right", {"start": v(-183.02, 26.96) * mm, "end": v(-183.02, 6.8) * mm, "construction": true});
            skPoint(sketch, "E190", {"position": v(-161.49, 27.96) * mm});
            skPoint(sketch, "E191", {"position": v(-183.9, 27.96) * mm});
            skPoint(sketch, "E192", {"position": v(-161.86, 5.56) * mm});
            skPoint(sketch, "E193", {"position": v(-183.77, 5.68) * mm});
            skLineSegment(sketch, "E194.bottom", {"start": v(-59.78, -5.67) * mm, "end": v(-80.07, -5.67) * mm, "construction": true});
            skLineSegment(sketch, "E194.top", {"start": v(-59.78, -25.83) * mm, "end": v(-80.07, -25.83) * mm, "construction": true});
            skLineSegment(sketch, "E194.left", {"start": v(-59.78, -5.67) * mm, "end": v(-59.78, -25.83) * mm, "construction": true});
            skLineSegment(sketch, "E194.right", {"start": v(-80.07, -5.67) * mm, "end": v(-80.07, -25.83) * mm, "construction": true});
            skPoint(sketch, "E195", {"position": v(-58.53, -4.67) * mm});
            skPoint(sketch, "E196", {"position": v(-80.94, -4.67) * mm});
            skPoint(sketch, "E197", {"position": v(-58.9, -27.08) * mm});
            skPoint(sketch, "E198", {"position": v(-80.82, -26.95) * mm});
            skLineSegment(sketch, "E199.bottom", {"start": v(-85.9, -5.67) * mm, "end": v(-106.17, -5.67) * mm, "construction": true});
            skLineSegment(sketch, "E199.top", {"start": v(-85.9, -25.83) * mm, "end": v(-106.17, -25.83) * mm, "construction": true});
            skLineSegment(sketch, "E199.left", {"start": v(-85.9, -5.67) * mm, "end": v(-85.9, -25.83) * mm, "construction": true});
            skLineSegment(sketch, "E199.right", {"start": v(-106.17, -5.67) * mm, "end": v(-106.17, -25.83) * mm, "construction": true});
            skPoint(sketch, "E200", {"position": v(-84.64, -4.67) * mm});
            skPoint(sketch, "E201", {"position": v(-107.05, -4.67) * mm});
            skPoint(sketch, "E202", {"position": v(-85.02, -27.08) * mm});
            skPoint(sketch, "E203", {"position": v(-106.92, -26.95) * mm});
            skLineSegment(sketch, "E204.bottom", {"start": v(-111.37, -5.67) * mm, "end": v(-131.65, -5.67) * mm, "construction": true});
            skLineSegment(sketch, "E204.top", {"start": v(-111.37, -25.83) * mm, "end": v(-131.65, -25.83) * mm, "construction": true});
            skLineSegment(sketch, "E204.left", {"start": v(-111.37, -5.67) * mm, "end": v(-111.37, -25.83) * mm, "construction": true});
            skLineSegment(sketch, "E204.right", {"start": v(-131.65, -5.67) * mm, "end": v(-131.65, -25.83) * mm, "construction": true});
            skPoint(sketch, "E205", {"position": v(-110.12, -4.67) * mm});
            skPoint(sketch, "E206", {"position": v(-132.52, -4.67) * mm});
            skPoint(sketch, "E207", {"position": v(-110.5, -27.08) * mm});
            skPoint(sketch, "E208", {"position": v(-132.4, -26.95) * mm});
            skLineSegment(sketch, "E209.bottom", {"start": v(-136.84, -5.88) * mm, "end": v(-157.12, -5.88) * mm, "construction": true});
            skLineSegment(sketch, "E209.top", {"start": v(-136.84, -26.04) * mm, "end": v(-157.12, -26.04) * mm, "construction": true});
            skLineSegment(sketch, "E209.left", {"start": v(-136.84, -5.88) * mm, "end": v(-136.84, -26.04) * mm, "construction": true});
            skLineSegment(sketch, "E209.right", {"start": v(-157.12, -5.88) * mm, "end": v(-157.12, -26.04) * mm, "construction": true});
            skPoint(sketch, "E210", {"position": v(-135.6, -4.88) * mm});
            skPoint(sketch, "E211", {"position": v(-158, -4.88) * mm});
            skPoint(sketch, "E212", {"position": v(-135.97, -27.29) * mm});
            skPoint(sketch, "E213", {"position": v(-157.88, -27.16) * mm});
            skLineSegment(sketch, "E214.bottom", {"start": v(-162.74, -5.88) * mm, "end": v(-183.02, -5.88) * mm, "construction": true});
            skLineSegment(sketch, "E214.top", {"start": v(-162.74, -26.04) * mm, "end": v(-183.02, -26.04) * mm, "construction": true});
            skLineSegment(sketch, "E214.left", {"start": v(-162.74, -5.88) * mm, "end": v(-162.74, -26.04) * mm, "construction": true});
            skLineSegment(sketch, "E214.right", {"start": v(-183.02, -5.88) * mm, "end": v(-183.02, -26.04) * mm, "construction": true});
            skPoint(sketch, "E215", {"position": v(-161.49, -4.88) * mm});
            skPoint(sketch, "E216", {"position": v(-183.9, -4.88) * mm});
            skPoint(sketch, "E217", {"position": v(-161.86, -27.29) * mm});
            skPoint(sketch, "E218", {"position": v(-183.77, -27.16) * mm});
            skLineSegment(sketch, "E219.bottom", {"start": v(-60.2, -38.73) * mm, "end": v(-80.49, -38.73) * mm, "construction": true});
            skLineSegment(sketch, "E219.top", {"start": v(-60.2, -58.88) * mm, "end": v(-80.49, -58.88) * mm, "construction": true});
            skLineSegment(sketch, "E219.left", {"start": v(-60.2, -38.73) * mm, "end": v(-60.2, -58.88) * mm, "construction": true});
            skLineSegment(sketch, "E219.right", {"start": v(-80.49, -38.73) * mm, "end": v(-80.49, -58.88) * mm, "construction": true});
            skPoint(sketch, "E220", {"position": v(-58.95, -37.73) * mm});
            skPoint(sketch, "E221", {"position": v(-81.36, -37.73) * mm});
            skPoint(sketch, "E222", {"position": v(-59.33, -60.13) * mm});
            skPoint(sketch, "E223", {"position": v(-81.24, -60) * mm});
            skLineSegment(sketch, "E224.bottom", {"start": v(-85.68, -38.73) * mm, "end": v(-105.96, -38.73) * mm, "construction": true});
            skLineSegment(sketch, "E224.top", {"start": v(-85.68, -58.88) * mm, "end": v(-105.96, -58.88) * mm, "construction": true});
            skLineSegment(sketch, "E224.left", {"start": v(-85.68, -38.73) * mm, "end": v(-85.68, -58.88) * mm, "construction": true});
            skLineSegment(sketch, "E224.right", {"start": v(-105.96, -38.73) * mm, "end": v(-105.96, -58.88) * mm, "construction": true});
            skPoint(sketch, "E225", {"position": v(-84.43, -37.73) * mm});
            skPoint(sketch, "E226", {"position": v(-106.84, -37.73) * mm});
            skPoint(sketch, "E227", {"position": v(-84.8, -60.13) * mm});
            skPoint(sketch, "E228", {"position": v(-106.71, -60) * mm});
            skLineSegment(sketch, "E229.bottom", {"start": v(-111.37, -38.73) * mm, "end": v(-131.65, -38.73) * mm, "construction": true});
            skLineSegment(sketch, "E229.top", {"start": v(-111.37, -58.88) * mm, "end": v(-131.65, -58.88) * mm, "construction": true});
            skLineSegment(sketch, "E229.left", {"start": v(-111.37, -38.73) * mm, "end": v(-111.37, -58.88) * mm, "construction": true});
            skLineSegment(sketch, "E229.right", {"start": v(-131.65, -38.73) * mm, "end": v(-131.65, -58.88) * mm, "construction": true});
            skPoint(sketch, "E230", {"position": v(-110.12, -37.73) * mm});
            skPoint(sketch, "E231", {"position": v(-132.52, -37.73) * mm});
            skPoint(sketch, "E232", {"position": v(-110.5, -60.13) * mm});
            skPoint(sketch, "E233", {"position": v(-132.4, -60) * mm});
            skLineSegment(sketch, "E234.bottom", {"start": v(-136.84, -38.73) * mm, "end": v(-157.12, -38.73) * mm, "construction": true});
            skLineSegment(sketch, "E234.top", {"start": v(-136.84, -58.88) * mm, "end": v(-157.12, -58.88) * mm, "construction": true});
            skLineSegment(sketch, "E234.left", {"start": v(-136.84, -38.73) * mm, "end": v(-136.84, -58.88) * mm, "construction": true});
            skLineSegment(sketch, "E234.right", {"start": v(-157.12, -38.73) * mm, "end": v(-157.12, -58.88) * mm, "construction": true});
            skPoint(sketch, "E235", {"position": v(-135.6, -37.73) * mm});
            skPoint(sketch, "E236", {"position": v(-158, -37.73) * mm});
            skPoint(sketch, "E237", {"position": v(-135.97, -60.13) * mm});
            skPoint(sketch, "E238", {"position": v(-157.88, -60) * mm});
            skLineSegment(sketch, "E239.bottom", {"start": v(172.05, 62.53) * mm, "end": v(145.94, 62.53) * mm, "construction": true});
            skLineSegment(sketch, "E239.top", {"start": v(172.05, 36.42) * mm, "end": v(145.94, 36.42) * mm, "construction": true});
            skLineSegment(sketch, "E239.left", {"start": v(172.05, 62.53) * mm, "end": v(172.05, 36.42) * mm, "construction": true});
            skLineSegment(sketch, "E239.right", {"start": v(145.94, 62.53) * mm, "end": v(145.94, 36.42) * mm, "construction": true});
            skPoint(sketch, "E240", {"position": v(173.95, 64.63) * mm});
            skPoint(sketch, "E241", {"position": v(144.47, 64.42) * mm});
            skPoint(sketch, "E242", {"position": v(174.58, 34.52) * mm});
            skPoint(sketch, "E243", {"position": v(143.63, 34.52) * mm});
            skLineSegment(sketch, "E244.bottom", {"start": v(135.55, 62.5) * mm, "end": v(109.44, 62.5) * mm, "construction": true});
            skLineSegment(sketch, "E244.top", {"start": v(135.55, 36.4) * mm, "end": v(109.44, 36.4) * mm, "construction": true});
            skLineSegment(sketch, "E244.left", {"start": v(135.55, 62.5) * mm, "end": v(135.55, 36.4) * mm, "construction": true});
            skLineSegment(sketch, "E244.right", {"start": v(109.44, 62.5) * mm, "end": v(109.44, 36.4) * mm, "construction": true});
            skPoint(sketch, "E245", {"position": v(137.44, 64.6) * mm});
            skPoint(sketch, "E246", {"position": v(107.97, 64.4) * mm});
            skPoint(sketch, "E247", {"position": v(138.07, 34.5) * mm});
            skPoint(sketch, "E248", {"position": v(107.12, 34.5) * mm});
            skLineSegment(sketch, "E249.bottom", {"start": v(98.07, 62.29) * mm, "end": v(71.96, 62.29) * mm, "construction": true});
            skLineSegment(sketch, "E249.top", {"start": v(98.07, 36.18) * mm, "end": v(71.96, 36.18) * mm, "construction": true});
            skLineSegment(sketch, "E249.left", {"start": v(98.07, 62.29) * mm, "end": v(98.07, 36.18) * mm, "construction": true});
            skLineSegment(sketch, "E249.right", {"start": v(71.96, 62.29) * mm, "end": v(71.96, 36.18) * mm, "construction": true});
            skPoint(sketch, "E250", {"position": v(99.97, 64.4) * mm});
            skPoint(sketch, "E251", {"position": v(70.5, 64.18) * mm});
            skPoint(sketch, "E252", {"position": v(100.6, 34.29) * mm});
            skPoint(sketch, "E253", {"position": v(69.65, 34.29) * mm});
            skLineSegment(sketch, "E254.bottom", {"start": v(13.11, 62.1) * mm, "end": v(-13, 62.1) * mm, "construction": true});
            skLineSegment(sketch, "E254.top", {"start": v(13.11, 35.99) * mm, "end": v(-13, 35.99) * mm, "construction": true});
            skLineSegment(sketch, "E254.left", {"start": v(13.11, 62.1) * mm, "end": v(13.11, 35.99) * mm, "construction": true});
            skLineSegment(sketch, "E254.right", {"start": v(-13, 62.1) * mm, "end": v(-13, 35.99) * mm, "construction": true});
            skPoint(sketch, "E255", {"position": v(15, 64.2) * mm});
            skPoint(sketch, "E256", {"position": v(-14.47, 64) * mm});
            skPoint(sketch, "E257", {"position": v(15.64, 34.1) * mm});
            skPoint(sketch, "E258", {"position": v(-15.3, 34.1) * mm});
            skLineSegment(sketch, "E259.bottom", {"start": v(-108.3, 62.1) * mm, "end": v(-134.4, 62.1) * mm, "construction": true});
            skLineSegment(sketch, "E259.top", {"start": v(-108.3, 35.99) * mm, "end": v(-134.4, 35.99) * mm, "construction": true});
            skLineSegment(sketch, "E259.left", {"start": v(-108.3, 62.1) * mm, "end": v(-108.3, 35.99) * mm, "construction": true});
            skLineSegment(sketch, "E259.right", {"start": v(-134.4, 62.1) * mm, "end": v(-134.4, 35.99) * mm, "construction": true});
            skPoint(sketch, "E260", {"position": v(-106.4, 64.2) * mm});
            skPoint(sketch, "E261", {"position": v(-135.88, 64) * mm});
            skPoint(sketch, "E262", {"position": v(-105.77, 34.1) * mm});
            skPoint(sketch, "E263", {"position": v(-136.72, 34.1) * mm});
            skLineSegment(sketch, "E264.bottom", {"start": v(6.67, 11.63) * mm, "end": v(-6.8, 11.63) * mm, "construction": true});
            skLineSegment(sketch, "E264.top", {"start": v(6.67, -1.72) * mm, "end": v(-6.8, -1.72) * mm, "construction": true});
            skLineSegment(sketch, "E264.left", {"start": v(6.67, 11.63) * mm, "end": v(6.67, -1.72) * mm, "construction": true});
            skLineSegment(sketch, "E264.right", {"start": v(-6.8, 11.63) * mm, "end": v(-6.8, -1.72) * mm, "construction": true});
            skPoint(sketch, "E265", {"position": v(6.67, 11.63) * mm});
            skPoint(sketch, "E266", {"position": v(-6.8, 11.63) * mm});
            skPoint(sketch, "E267", {"position": v(6.67, -1.72) * mm});
            skPoint(sketch, "E268", {"position": v(-6.75, -1.78) * mm});
            skSolve(sketch);
        }
        {
            var Q0;
            Q0=sQuery(id+"F18.wireOp",VERTEX,"E240");
            var Q1;
            Q1=sQuery(id+"F18.wireOp",VERTEX,"E241");
            var Q2;
            Q2=sQuery(id+"F18.wireOp",VERTEX,"E245");
            var Q3;
            Q3=sQuery(id+"F18.wireOp",VERTEX,"E246");
            var Q4;
            Q4=sQuery(id+"F18.wireOp",VERTEX,"E250");
            var Q5;
            Q5=sQuery(id+"F18.wireOp",VERTEX,"E251");
            var Q6;
            Q6=sQuery(id+"F18.wireOp",VERTEX,"E253");
            var Q7;
            Q7=sQuery(id+"F18.wireOp",VERTEX,"E252");
            var Q8;
            Q8=sQuery(id+"F18.wireOp",VERTEX,"E248");
            var Q9;
            Q9=sQuery(id+"F18.wireOp",VERTEX,"E247");
            var Q10;
            Q10=sQuery(id+"F18.wireOp",VERTEX,"E243");
            var Q11;
            Q11=sQuery(id+"F18.wireOp",VERTEX,"E242");
            var Q12;
            Q12=sQuery(id+"F18.wireOp",VERTEX,"E80");
            var Q13;
            Q13=sQuery(id+"F18.wireOp",VERTEX,"E82");
            var Q14;
            Q14=sQuery(id+"F18.wireOp",VERTEX,"E83");
            var Q15;
            Q15=sQuery(id+"F18.wireOp",VERTEX,"E81");
            var Q16;
            Q16=sQuery(id+"F18.wireOp",VERTEX,"E85");
            var Q17;
            Q17=sQuery(id+"F18.wireOp",VERTEX,"E87");
            var Q18;
            Q18=sQuery(id+"F18.wireOp",VERTEX,"E88");
            var Q19;
            Q19=sQuery(id+"F18.wireOp",VERTEX,"E86");
            var Q20;
            Q20=sQuery(id+"F18.wireOp",VERTEX,"E90");
            var Q21;
            Q21=sQuery(id+"F18.wireOp",VERTEX,"E92");
            var Q22;
            Q22=sQuery(id+"F18.wireOp",VERTEX,"E93");
            var Q23;
            Q23=sQuery(id+"F18.wireOp",VERTEX,"E91");
            var Q24;
            Q24=sQuery(id+"F18.wireOp",VERTEX,"E95");
            var Q25;
            Q25=sQuery(id+"F18.wireOp",VERTEX,"E97");
            var Q26;
            Q26=sQuery(id+"F18.wireOp",VERTEX,"E98");
            var Q27;
            Q27=sQuery(id+"F18.wireOp",VERTEX,"E96");
            var Q28;
            Q28=sQuery(id+"F18.wireOp",VERTEX,"E100");
            var Q29;
            Q29=sQuery(id+"F18.wireOp",VERTEX,"E102");
            var Q30;
            Q30=sQuery(id+"F18.wireOp",VERTEX,"E103");
            var Q31;
            Q31=sQuery(id+"F18.wireOp",VERTEX,"E101");
            var Q32;
            Q32=sQuery(id+"F18.wireOp",VERTEX,"E105");
            var Q33;
            Q33=sQuery(id+"F18.wireOp",VERTEX,"E106");
            var Q34;
            Q34=sQuery(id+"F18.wireOp",VERTEX,"E107");
            var Q35;
            Q35=sQuery(id+"F18.wireOp",VERTEX,"E108");
            var Q36;
            Q36=sQuery(id+"F18.wireOp",VERTEX,"E112");
            var Q37;
            Q37=sQuery(id+"F18.wireOp",VERTEX,"E110");
            var Q38;
            Q38=sQuery(id+"F18.wireOp",VERTEX,"E111");
            var Q39;
            Q39=sQuery(id+"F18.wireOp",VERTEX,"E113");
            var Q40;
            Q40=sQuery(id+"F18.wireOp",VERTEX,"E115");
            var Q41;
            Q41=sQuery(id+"F18.wireOp",VERTEX,"E116");
            var Q42;
            Q42=sQuery(id+"F18.wireOp",VERTEX,"E118");
            var Q43;
            Q43=sQuery(id+"F18.wireOp",VERTEX,"E122");
            var Q44;
            Q44=sQuery(id+"F18.wireOp",VERTEX,"E120");
            var Q45;
            Q45=sQuery(id+"F18.wireOp",VERTEX,"E121");
            var Q46;
            Q46=sQuery(id+"F18.wireOp",VERTEX,"E123");
            var Q47;
            Q47=sQuery(id+"F18.wireOp",VERTEX,"E125");
            var Q48;
            Q48=sQuery(id+"F18.wireOp",VERTEX,"E127");
            var Q49;
            Q49=sQuery(id+"F18.wireOp",VERTEX,"E128");
            var Q50;
            Q50=sQuery(id+"F18.wireOp",VERTEX,"E126");
            var Q51;
            Q51=sQuery(id+"F18.wireOp",VERTEX,"E117");
            var Q52;
            Q52=makeQuery(id+"F1.opExtrude","SWEPT_BODY",BODY,{"disambiguationData":[OSD([sQuery(id+"F0.wireOp",EDGE,"E0.bottom"),sQuery(id+"F0.wireOp",EDGE,"E0.top"),sQuery(id+"F0.wireOp",EDGE,"E0.left"),sQuery(id+"F0.wireOp",EDGE,"E0.right")])]});
            hole(context, id + "F19", {"style" : HoleStyle.SIMPLE, "endStyle" : HoleEndStyle.BLIND, "holeDiameter" : 2 * mm, "holeDepth" : 20 * mm, "locations" : qUnion([Q0, Q1, Q2, Q3, Q4, Q5, Q6, Q7, Q8, Q9, Q10, Q11, Q12, Q13, Q14, Q15, Q16, Q17, Q18, Q19, Q20, Q21, Q22, Q23, Q24, Q25, Q26, Q27, Q28, Q29, Q30, Q31, Q32, Q33, Q34, Q35, Q36, Q37, Q38, Q39, Q40, Q41, Q42, Q43, Q44, Q45, Q46, Q47, Q48, Q49, Q50, Q51]), "scope" : qUnion([Q52])});
        }
        {
            var Q0;
            Q0=sQuery(id+"F18.wireOp",VERTEX,"E130");
            var Q1;
            Q1=sQuery(id+"F18.wireOp",VERTEX,"E132");
            var Q2;
            Q2=sQuery(id+"F18.wireOp",VERTEX,"E131");
            var Q3;
            Q3=sQuery(id+"F18.wireOp",VERTEX,"E133");
            var Q4;
            Q4=sQuery(id+"F18.wireOp",VERTEX,"E135");
            var Q5;
            Q5=sQuery(id+"F18.wireOp",VERTEX,"E137");
            var Q6;
            Q6=sQuery(id+"F18.wireOp",VERTEX,"E138");
            var Q7;
            Q7=sQuery(id+"F18.wireOp",VERTEX,"E136");
            var Q8;
            Q8=sQuery(id+"F18.wireOp",VERTEX,"E140");
            var Q9;
            Q9=sQuery(id+"F18.wireOp",VERTEX,"E142");
            var Q10;
            Q10=sQuery(id+"F18.wireOp",VERTEX,"E143");
            var Q11;
            Q11=sQuery(id+"F18.wireOp",VERTEX,"E141");
            var Q12;
            Q12=sQuery(id+"F18.wireOp",VERTEX,"E145");
            var Q13;
            Q13=sQuery(id+"F18.wireOp",VERTEX,"E147");
            var Q14;
            Q14=sQuery(id+"F18.wireOp",VERTEX,"E146");
            var Q15;
            Q15=sQuery(id+"F18.wireOp",VERTEX,"E148");
            var Q16;
            Q16=sQuery(id+"F18.wireOp",VERTEX,"E255");
            var Q17;
            Q17=sQuery(id+"F18.wireOp",VERTEX,"E257");
            var Q18;
            Q18=sQuery(id+"F18.wireOp",VERTEX,"E258");
            var Q19;
            Q19=sQuery(id+"F18.wireOp",VERTEX,"E256");
            var Q20;
            Q20=sQuery(id+"F18.wireOp",VERTEX,"E220");
            var Q21;
            Q21=sQuery(id+"F18.wireOp",VERTEX,"E222");
            var Q22;
            Q22=sQuery(id+"F18.wireOp",VERTEX,"E221");
            var Q23;
            Q23=sQuery(id+"F18.wireOp",VERTEX,"E223");
            var Q24;
            Q24=sQuery(id+"F18.wireOp",VERTEX,"E227");
            var Q25;
            Q25=sQuery(id+"F18.wireOp",VERTEX,"E225");
            var Q26;
            Q26=sQuery(id+"F18.wireOp",VERTEX,"E226");
            var Q27;
            Q27=sQuery(id+"F18.wireOp",VERTEX,"E228");
            var Q28;
            Q28=sQuery(id+"F18.wireOp",VERTEX,"E232");
            var Q29;
            Q29=sQuery(id+"F18.wireOp",VERTEX,"E230");
            var Q30;
            Q30=sQuery(id+"F18.wireOp",VERTEX,"E231");
            var Q31;
            Q31=sQuery(id+"F18.wireOp",VERTEX,"E233");
            var Q32;
            Q32=sQuery(id+"F18.wireOp",VERTEX,"E237");
            var Q33;
            Q33=sQuery(id+"F18.wireOp",VERTEX,"E235");
            var Q34;
            Q34=sQuery(id+"F18.wireOp",VERTEX,"E236");
            var Q35;
            Q35=sQuery(id+"F18.wireOp",VERTEX,"E238");
            var Q36;
            Q36=sQuery(id+"F18.wireOp",VERTEX,"E265");
            var Q37;
            Q37=sQuery(id+"F18.wireOp",VERTEX,"E266");
            var Q38;
            Q38=sQuery(id+"F18.wireOp",VERTEX,"E267");
            var Q39;
            Q39=sQuery(id+"F18.wireOp",VERTEX,"E268");
            var Q40;
            Q40=makeQuery(id+"F1.opExtrude","SWEPT_BODY",BODY,{"disambiguationData":[OSD([sQuery(id+"F0.wireOp",EDGE,"E0.bottom"),sQuery(id+"F0.wireOp",EDGE,"E0.top"),sQuery(id+"F0.wireOp",EDGE,"E0.left"),sQuery(id+"F0.wireOp",EDGE,"E0.right")])]});
            hole(context, id + "F20", {"style" : HoleStyle.SIMPLE, "endStyle" : HoleEndStyle.BLIND, "holeDiameter" : 2 * mm, "holeDepth" : 20 * mm, "locations" : qUnion([Q0, Q1, Q2, Q3, Q4, Q5, Q6, Q7, Q8, Q9, Q10, Q11, Q12, Q13, Q14, Q15, Q16, Q17, Q18, Q19, Q20, Q21, Q22, Q23, Q24, Q25, Q26, Q27, Q28, Q29, Q30, Q31, Q32, Q33, Q34, Q35, Q36, Q37, Q38, Q39]), "scope" : qUnion([Q40])});
        }
        {
            var Q0;
            Q0=sQuery(id+"F18.wireOp",VERTEX,"E150");
            var Q1;
            Q1=sQuery(id+"F18.wireOp",VERTEX,"E151");
            var Q2;
            Q2=sQuery(id+"F18.wireOp",VERTEX,"E152");
            var Q3;
            Q3=sQuery(id+"F18.wireOp",VERTEX,"E153");
            var Q4;
            Q4=sQuery(id+"F18.wireOp",VERTEX,"E155");
            var Q5;
            Q5=sQuery(id+"F18.wireOp",VERTEX,"E156");
            var Q6;
            Q6=sQuery(id+"F18.wireOp",VERTEX,"E157");
            var Q7;
            Q7=sQuery(id+"F18.wireOp",VERTEX,"E158");
            var Q8;
            Q8=sQuery(id+"F18.wireOp",VERTEX,"E260");
            var Q9;
            Q9=sQuery(id+"F18.wireOp",VERTEX,"E261");
            var Q10;
            Q10=sQuery(id+"F18.wireOp",VERTEX,"E262");
            var Q11;
            Q11=sQuery(id+"F18.wireOp",VERTEX,"E263");
            var Q12;
            Q12=sQuery(id+"F18.wireOp",VERTEX,"E162");
            var Q13;
            Q13=sQuery(id+"F18.wireOp",VERTEX,"E160");
            var Q14;
            Q14=sQuery(id+"F18.wireOp",VERTEX,"E161");
            var Q15;
            Q15=sQuery(id+"F18.wireOp",VERTEX,"E163");
            var Q16;
            Q16=sQuery(id+"F18.wireOp",VERTEX,"E167");
            var Q17;
            Q17=sQuery(id+"F18.wireOp",VERTEX,"E165");
            var Q18;
            Q18=sQuery(id+"F18.wireOp",VERTEX,"E166");
            var Q19;
            Q19=sQuery(id+"F18.wireOp",VERTEX,"E170");
            var Q20;
            Q20=sQuery(id+"F18.wireOp",VERTEX,"E171");
            var Q21;
            Q21=sQuery(id+"F18.wireOp",VERTEX,"E172");
            var Q22;
            Q22=sQuery(id+"F18.wireOp",VERTEX,"E173");
            var Q23;
            Q23=sQuery(id+"F18.wireOp",VERTEX,"E175");
            var Q24;
            Q24=sQuery(id+"F18.wireOp",VERTEX,"E176");
            var Q25;
            Q25=sQuery(id+"F18.wireOp",VERTEX,"E177");
            var Q26;
            Q26=sQuery(id+"F18.wireOp",VERTEX,"E178");
            var Q27;
            Q27=sQuery(id+"F18.wireOp",VERTEX,"E180");
            var Q28;
            Q28=sQuery(id+"F18.wireOp",VERTEX,"E181");
            var Q29;
            Q29=sQuery(id+"F18.wireOp",VERTEX,"E182");
            var Q30;
            Q30=sQuery(id+"F18.wireOp",VERTEX,"E183");
            var Q31;
            Q31=sQuery(id+"F18.wireOp",VERTEX,"E185");
            var Q32;
            Q32=sQuery(id+"F18.wireOp",VERTEX,"E186");
            var Q33;
            Q33=sQuery(id+"F18.wireOp",VERTEX,"E187");
            var Q34;
            Q34=sQuery(id+"F18.wireOp",VERTEX,"E188");
            var Q35;
            Q35=sQuery(id+"F18.wireOp",VERTEX,"E190");
            var Q36;
            Q36=sQuery(id+"F18.wireOp",VERTEX,"E191");
            var Q37;
            Q37=sQuery(id+"F18.wireOp",VERTEX,"E192");
            var Q38;
            Q38=sQuery(id+"F18.wireOp",VERTEX,"E193");
            var Q39;
            Q39=sQuery(id+"F18.wireOp",VERTEX,"E195");
            var Q40;
            Q40=sQuery(id+"F18.wireOp",VERTEX,"E197");
            var Q41;
            Q41=sQuery(id+"F18.wireOp",VERTEX,"E196");
            var Q42;
            Q42=sQuery(id+"F18.wireOp",VERTEX,"E198");
            var Q43;
            Q43=sQuery(id+"F18.wireOp",VERTEX,"E200");
            var Q44;
            Q44=sQuery(id+"F18.wireOp",VERTEX,"E202");
            var Q45;
            Q45=sQuery(id+"F18.wireOp",VERTEX,"E201");
            var Q46;
            Q46=sQuery(id+"F18.wireOp",VERTEX,"E203");
            var Q47;
            Q47=sQuery(id+"F18.wireOp",VERTEX,"E205");
            var Q48;
            Q48=sQuery(id+"F18.wireOp",VERTEX,"E207");
            var Q49;
            Q49=sQuery(id+"F18.wireOp",VERTEX,"E206");
            var Q50;
            Q50=sQuery(id+"F18.wireOp",VERTEX,"E208");
            var Q51;
            Q51=sQuery(id+"F18.wireOp",VERTEX,"E210");
            var Q52;
            Q52=sQuery(id+"F18.wireOp",VERTEX,"E212");
            var Q53;
            Q53=sQuery(id+"F18.wireOp",VERTEX,"E211");
            var Q54;
            Q54=sQuery(id+"F18.wireOp",VERTEX,"E213");
            var Q55;
            Q55=sQuery(id+"F18.wireOp",VERTEX,"E217");
            var Q56;
            Q56=sQuery(id+"F18.wireOp",VERTEX,"E215");
            var Q57;
            Q57=sQuery(id+"F18.wireOp",VERTEX,"E216");
            var Q58;
            Q58=sQuery(id+"F18.wireOp",VERTEX,"E218");
            var Q59;
            Q59=makeQuery(id+"F1.opExtrude","SWEPT_BODY",BODY,{"disambiguationData":[OSD([sQuery(id+"F0.wireOp",EDGE,"E0.bottom"),sQuery(id+"F0.wireOp",EDGE,"E0.top"),sQuery(id+"F0.wireOp",EDGE,"E0.left"),sQuery(id+"F0.wireOp",EDGE,"E0.right")])]});
            hole(context, id + "F21", {"style" : HoleStyle.SIMPLE, "endStyle" : HoleEndStyle.BLIND, "holeDiameter" : 2 * mm, "holeDepth" : 20 * mm, "locations" : qUnion([Q0, Q1, Q2, Q3, Q4, Q5, Q6, Q7, Q8, Q9, Q10, Q11, Q12, Q13, Q14, Q15, Q16, Q17, Q18, Q19, Q20, Q21, Q22, Q23, Q24, Q25, Q26, Q27, Q28, Q29, Q30, Q31, Q32, Q33, Q34, Q35, Q36, Q37, Q38, Q39, Q40, Q41, Q42, Q43, Q44, Q45, Q46, Q47, Q48, Q49, Q50, Q51, Q52, Q53, Q54, Q55, Q56, Q57, Q58]), "scope" : qUnion([Q59])});
        }
        {
            var Q0;
            Q0=makeQuery(id+"F15.boolean.opBoolean","COPY",EDGE,{"derivedFrom":makeQuery(id+"F15.opExtrude","SWEPT_EDGE",EDGE,{"disambiguationData":[OSD([sQuery(id+"F9.wireOp",EDGE,"E40.bottom"),sQuery(id+"F9.wireOp",EDGE,"E40.left")])]})});
            var Q1;
            Q1=makeQuery(id+"F15.boolean.opBoolean","COPY",EDGE,{"derivedFrom":makeQuery(id+"F15.opExtrude","SWEPT_EDGE",EDGE,{"disambiguationData":[OSD([sQuery(id+"F9.wireOp",EDGE,"E40.bottom"),sQuery(id+"F9.wireOp",EDGE,"E40.right")])]})});
            var Q2;
            Q2=makeQuery(id+"F15.boolean.opBoolean","COPY",EDGE,{"derivedFrom":makeQuery(id+"F15.opExtrude","SWEPT_EDGE",EDGE,{"disambiguationData":[OSD([sQuery(id+"F9.wireOp",EDGE,"E40.top"),sQuery(id+"F9.wireOp",EDGE,"E40.right")])]})});
            var Q3;
            Q3=makeQuery(id+"F15.boolean.opBoolean","COPY",EDGE,{"derivedFrom":makeQuery(id+"F15.opExtrude","SWEPT_EDGE",EDGE,{"disambiguationData":[OSD([sQuery(id+"F9.wireOp",EDGE,"E40.top"),sQuery(id+"F9.wireOp",EDGE,"E40.left")])]})});
            fillet(context, id + "F22", {"entities" : qUnion([Q0, Q1, Q2, Q3]), "radius" : 5 * mm, "tangentPropagation" : true, "allowEdgeOverflow" : false});
        }
    });
